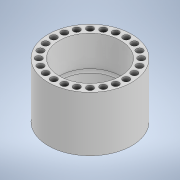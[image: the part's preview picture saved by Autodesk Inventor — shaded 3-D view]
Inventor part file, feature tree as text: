
AUTODESK INVENTOR PART (.ipt)
format: ipt  version: 2020 (Build 240168000, 168)  size: 174,080 bytes
history: native  units: in
note: dims shown in document units (in); Inventor stores cm internally (conversion verified against a paired STEP export)
features: extrude x3, sketch x3, pattern_circular x1, chamfer x1
ambient origin geometry x8: Origin, YZ Plane, XZ Plane, XY Plane, X Axis, Y Axis, Z Axis, Center Point
bodies: Solid1 (feature_tree)
feature tree (8):
  extrude  "Extrusion1"  Depth=1.1024in
  extrude  "Extrusion2"  Depth=0.9843in
  pattern_circular  "Circular Pattern1"  [2 undecoded]
  extrude  "Extrusion3"  Depth=0.9843in TaperAngle=360.0deg
  chamfer  "Chamfer1"  Distance=1.0236in
  sketch  "Sketch1"  dims[d0=1.4961in d1=1.1024in]
  sketch  "Sketch2"  dims[d2=0.9843in d3=0.0in d4=0.1181in]
  sketch  "Sketch3"  dims[d5=0.6496in d6=0.9843in d7=0.0in d8=9.4488in d9=360.0deg d11=1.0236in d12=0.4331in d13=0.0in d14=0.0394in d15=0.0787in d16=45.0deg]
note: 2 required parameter values undecoded (feature->parameter linkage not recoverable at this tier; creation-order binding heuristic only, values carry confidence <= 0.55)
